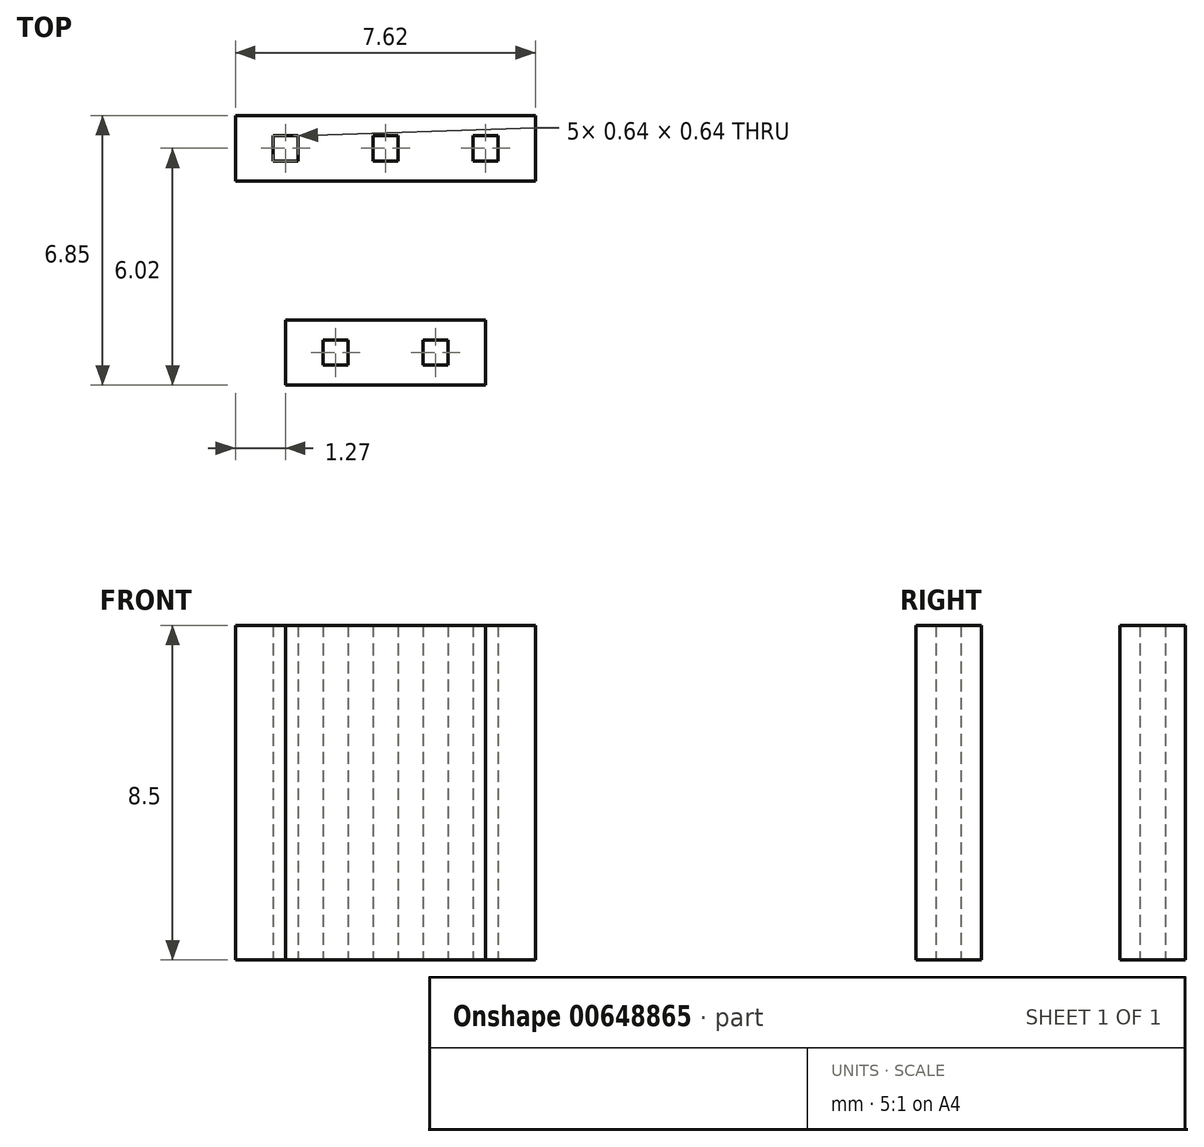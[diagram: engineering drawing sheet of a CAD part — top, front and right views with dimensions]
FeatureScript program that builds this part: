
annotation { "Feature Type Name" : "Feature", "Feature Type Description" : "" }
export const myFeature = defineFeature(function(context is Context, id is Id, definition is map)
    precondition{}
    {
        {
            var Q0;
            Q0=qCreatedBy(makeId("Top.planeOp"),FACE);
            var sketch = newSketch(context, id + "F0", { "sketchPlane" : qUnion([Q0])});
            skLineSegment(sketch, "E0.bottom", {"start": v(3.81, -0.83) * mm, "end": v(-3.81, -0.83) * mm});
            skLineSegment(sketch, "E0.top", {"start": v(3.8, 0.83) * mm, "end": v(-3.81, 0.83) * mm});
            skLineSegment(sketch, "E0.left", {"start": v(3.8, -0.83) * mm, "end": v(3.8, 0.83) * mm});
            skLineSegment(sketch, "E0.right", {"start": v(-3.81, -0.83) * mm, "end": v(-3.81, 0.83) * mm});
            skPoint(sketch, "E0.middle", {"position": v(0, 0) * mm});
            skLineSegment(sketch, "E1.bottom", {"start": v(0.32, -0.32) * mm, "end": v(-0.32, -0.32) * mm});
            skLineSegment(sketch, "E1.top", {"start": v(0.32, 0.32) * mm, "end": v(-0.32, 0.32) * mm});
            skLineSegment(sketch, "E1.left", {"start": v(0.32, -0.32) * mm, "end": v(0.32, 0.32) * mm});
            skLineSegment(sketch, "E1.right", {"start": v(-0.32, -0.32) * mm, "end": v(-0.32, 0.32) * mm});
            skLineSegment(sketch, "E2.1.0.0", {"start": v(2.86, -0.32) * mm, "end": v(2.86, 0.32) * mm});
            skLineSegment(sketch, "E2.1.0.1", {"start": v(2.86, 0.32) * mm, "end": v(2.22, 0.32) * mm});
            skLineSegment(sketch, "E2.1.0.2", {"start": v(2.22, -0.32) * mm, "end": v(2.22, 0.32) * mm});
            skLineSegment(sketch, "E2.1.0.3", {"start": v(2.86, -0.32) * mm, "end": v(2.22, -0.32) * mm});
            skPoint(sketch, "E2.1.0.4", {"position": v(2.54, 0) * mm});
            skLineSegment(sketch, "E3.1.0.0", {"start": v(-2.22, -0.32) * mm, "end": v(-2.86, -0.32) * mm});
            skLineSegment(sketch, "E3.1.0.1", {"start": v(-2.22, -0.32) * mm, "end": v(-2.22, 0.32) * mm});
            skLineSegment(sketch, "E3.1.0.2", {"start": v(-2.22, 0.32) * mm, "end": v(-2.86, 0.32) * mm});
            skLineSegment(sketch, "E3.1.0.3", {"start": v(-2.86, -0.32) * mm, "end": v(-2.86, 0.32) * mm});
            skPoint(sketch, "E3.1.0.4", {"position": v(-2.54, 0) * mm});
            skLineSegment(sketch, "E4.bottom", {"start": v(-2.54, -6.02) * mm, "end": v(2.54, -6.02) * mm});
            skLineSegment(sketch, "E4.top", {"start": v(-2.54, -4.36) * mm, "end": v(2.54, -4.36) * mm});
            skLineSegment(sketch, "E4.left", {"start": v(-2.54, -6.02) * mm, "end": v(-2.54, -4.36) * mm});
            skLineSegment(sketch, "E4.right", {"start": v(2.54, -6.02) * mm, "end": v(2.54, -4.36) * mm});
            skPoint(sketch, "E4.middle", {"position": v(0, -5.19) * mm});
            skLineSegment(sketch, "E5.bottom", {"start": v(0.95, -5.5) * mm, "end": v(1.6, -5.5) * mm});
            skLineSegment(sketch, "E5.top", {"start": v(0.95, -4.87) * mm, "end": v(1.6, -4.87) * mm});
            skLineSegment(sketch, "E5.left", {"start": v(0.95, -5.5) * mm, "end": v(0.95, -4.87) * mm});
            skLineSegment(sketch, "E5.right", {"start": v(1.6, -5.5) * mm, "end": v(1.6, -4.87) * mm});
            skPoint(sketch, "E5.middle", {"position": v(1.27, -5.19) * mm});
            skLineSegment(sketch, "E6.bottom", {"start": v(-1.59, -5.5) * mm, "end": v(-0.95, -5.5) * mm});
            skLineSegment(sketch, "E6.top", {"start": v(-1.59, -4.87) * mm, "end": v(-0.95, -4.87) * mm});
            skLineSegment(sketch, "E6.left", {"start": v(-1.59, -5.5) * mm, "end": v(-1.59, -4.87) * mm});
            skLineSegment(sketch, "E6.right", {"start": v(-0.95, -5.5) * mm, "end": v(-0.95, -4.87) * mm});
            skPoint(sketch, "E6.middle", {"position": v(-1.27, -5.19) * mm});
            skSolve(sketch);
        }
        {
            var Q0;
            Q0 = qSketchRegion(id + "F0", true);
            extrude(context, id + "F1", {"entities" : qUnion([Q0]), "depth" : 8.5 * mm, "offsetDistance" : 25 * mm});
        }
    });
